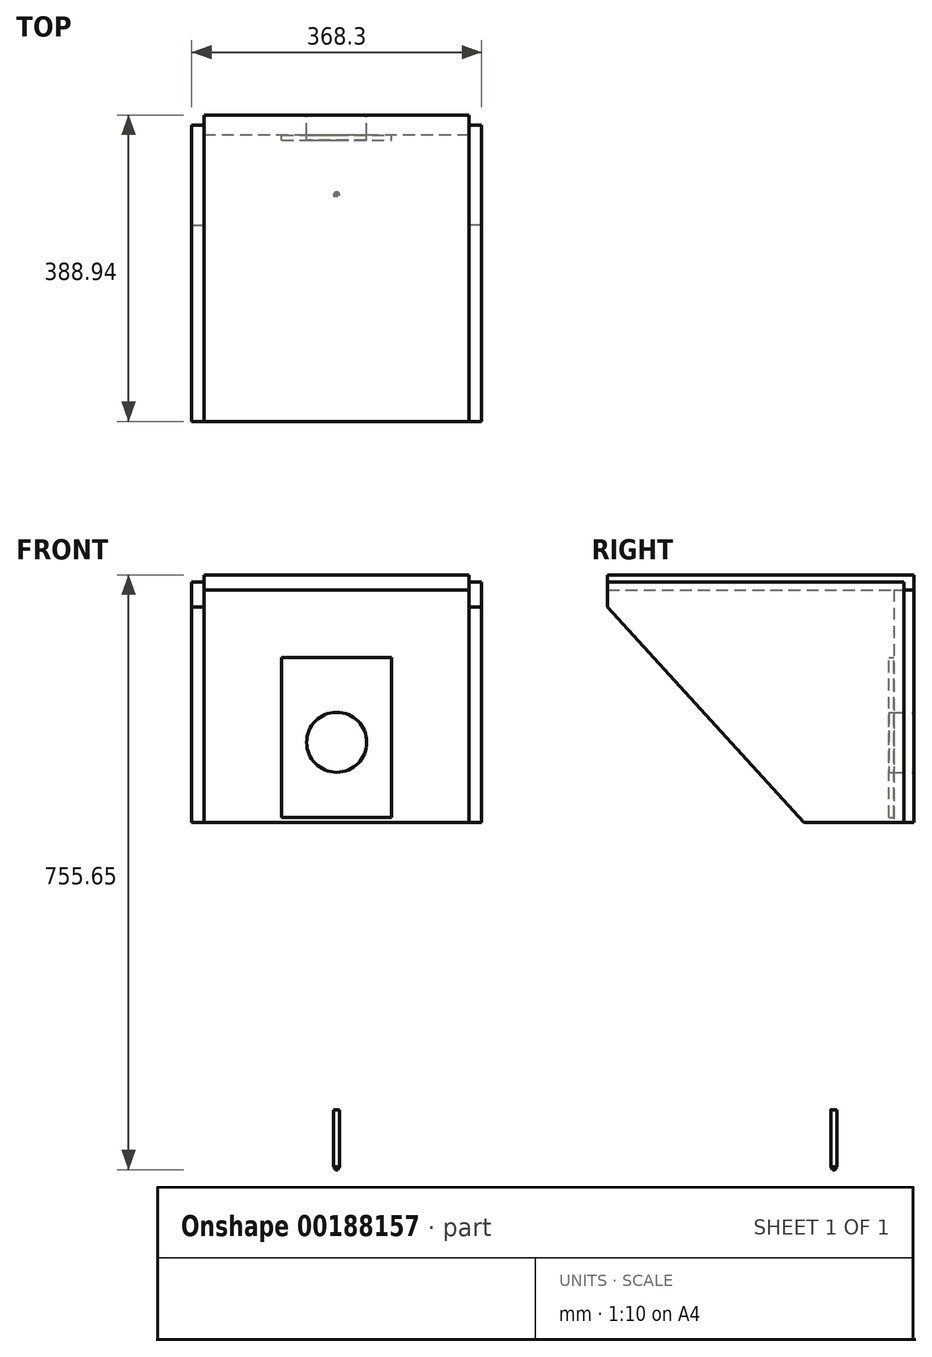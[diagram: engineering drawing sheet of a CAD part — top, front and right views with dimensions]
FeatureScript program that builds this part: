
annotation { "Feature Type Name" : "Feature", "Feature Type Description" : "" }
export const myFeature = defineFeature(function(context is Context, id is Id, definition is map)
    precondition{}
    {
        {
            var Q0;
            Q0=qCreatedBy(makeId("Top.planeOp"),FACE);
            var sketch = newSketch(context, id + "F0", { "sketchPlane" : qUnion([Q0])});
            skLineSegment(sketch, "E0.bottom", {"start": v(168.28, -194.47) * mm, "end": v(-168.28, -194.47) * mm});
            skLineSegment(sketch, "E0.top", {"start": v(168.28, 194.47) * mm, "end": v(-168.28, 194.47) * mm});
            skLineSegment(sketch, "E0.left", {"start": v(168.28, -194.47) * mm, "end": v(168.28, 194.47) * mm});
            skLineSegment(sketch, "E0.right", {"start": v(-168.28, -194.47) * mm, "end": v(-168.27, 194.47) * mm});
            skPoint(sketch, "E0.middle", {"position": v(0, 0) * mm});
            skSolve(sketch);
        }
        {
            var Q0;
            Q0=makeQuery(id+"F0.imprint","IMPRINT",FACE,{"disambiguationData":[TD([[makeQuery(id+"F0.imprint","IMPRINT",EDGE,{"derivedFrom":sQuery(id+"F0.wireOp",EDGE,"E0.bottom")}),-1.0]])]});
            extrude(context, id + "F1", {"entities" : qUnion([Q0]), "depth" : 19.05 * mm});
        }
        {
            var Q0;
            Q0=makeQuery(id+"F1.opExtrude","SWEPT_FACE",FACE,{"disambiguationData":[OSD([sQuery(id+"F0.wireOp",EDGE,"E0.top")])]});
            var sketch = newSketch(context, id + "F2", { "sketchPlane" : qUnion([Q0])});
            skLineSegment(sketch, "E1", {"start": v(-168.28, 0) * mm, "end": v(168.27, 0) * mm});
            skLineSegment(sketch, "E2", {"start": v(168.27, 0) * mm, "end": v(168.27, -295.28) * mm});
            skLineSegment(sketch, "E3", {"start": v(168.27, -295.28) * mm, "end": v(-168.28, -295.28) * mm});
            skLineSegment(sketch, "E4", {"start": v(-168.28, -295.27) * mm, "end": v(-168.28, 0) * mm});
            skCircle(sketch, "E5", {"center": v(0, -193.67) * mm, "radius": 38.1 * mm});
            skSolve(sketch);
        }
        {
            var Q0;
            Q0=makeQuery(id+"F2.imprint","IMPRINT",FACE,{"disambiguationData":[TD([[makeQuery(id+"F2.imprint","IMPRINT",EDGE,{"derivedFrom":sQuery(id+"F2.wireOp",EDGE,"E1")}),-1.0]])]});
            extrude(context, id + "F3", {"entities" : qUnion([Q0]), "oppositeDirection" : true, "depth" : 25.4 * mm});
        }
        {
            var Q0;
            Q0=makeQuery(id+"F1.opExtrude","SWEPT_FACE",FACE,{"disambiguationData":[OSD([sQuery(id+"F0.wireOp",EDGE,"E0.left")])]});
            var sketch = newSketch(context, id + "F4", { "sketchPlane" : qUnion([Q0])});
            skLineSegment(sketch, "E6", {"start": v(-194.47, 10.14) * mm, "end": v(-194.47, -21.61) * mm});
            skLineSegment(sketch, "E7", {"start": v(181.77, -295.27) * mm, "end": v(54.77, -295.27) * mm});
            skLineSegment(sketch, "E8", {"start": v(-194.47, -21.61) * mm, "end": v(54.77, -295.28) * mm});
            skLineSegment(sketch, "E9", {"start": v(-194.47, 10.14) * mm, "end": v(181.77, 10.14) * mm});
            skLineSegment(sketch, "E10", {"start": v(181.77, -295.27) * mm, "end": v(181.77, 10.14) * mm});
            skSolve(sketch);
        }
        {
            var Q0;
            Q0 = qSketchRegion(id + "F4", true);
            extrude(context, id + "F5", {"entities" : qUnion([Q0]), "depth" : 15.88 * mm});
        }
        {
            var Q0;
            Q0=makeQuery(id+"F5.opExtrude","SWEPT_BODY",BODY,{"disambiguationData":[OSD([sQuery(id+"F4.wireOp",EDGE,"E6"),sQuery(id+"F4.wireOp",EDGE,"E7"),sQuery(id+"F4.wireOp",EDGE,"E8"),sQuery(id+"F4.wireOp",EDGE,"E9"),sQuery(id+"F4.wireOp",EDGE,"E10")])]});
            var Q1;
            Q1=qCreatedBy(makeId("Right.planeOp"),FACE);
            mirror(context, id + "F6", {"entities" : qUnion([Q0]), "mirrorPlane" : qUnion([Q1])});
        }
        {
            var Q0;
            Q0=makeQuery(id+"F3.opExtrude","CAP_FACE",FACE,{"disambiguationData":[OSD([sQuery(id+"F2.wireOp",EDGE,"E1"),sQuery(id+"F2.wireOp",EDGE,"E2"),sQuery(id+"F2.wireOp",EDGE,"E3"),sQuery(id+"F2.wireOp",EDGE,"E4"),sQuery(id+"F2.wireOp",EDGE,"E5")])],"isStart":false});
            var sketch = newSketch(context, id + "F7", { "sketchPlane" : qUnion([Q0])});
            skLineSegment(sketch, "E11", {"start": v(-69.85, -288.93) * mm, "end": v(-69.85, -85.72) * mm});
            skLineSegment(sketch, "E12", {"start": v(-69.85, -288.93) * mm, "end": v(0, -288.93) * mm});
            skLineSegment(sketch, "E13", {"start": v(-69.85, -85.72) * mm, "end": v(0, -85.72) * mm});
            skLineSegment(sketch, "E14.MirrorCS", {"start": v(69.85, -288.93) * mm, "end": v(0, -288.93) * mm});
            skLineSegment(sketch, "E15.MirrorCS", {"start": v(69.85, -85.72) * mm, "end": v(0, -85.72) * mm});
            skLineSegment(sketch, "E16.MirrorCS", {"start": v(69.85, -288.93) * mm, "end": v(69.85, -85.72) * mm});
            skCircle(sketch, "E17", {"center": v(0, -193.67) * mm, "radius": 38.1 * mm});
            skSolve(sketch);
        }
        {
            var Q0;
            Q0 = qSketchRegion(id + "F7", true);
            extrude(context, id + "F8", {"entities" : qUnion([Q0]), "depth" : 6.35 * mm});
        }
        {
            var Q0;
            Q0=qCreatedBy(makeId("Right.planeOp"),FACE);
            var sketch = newSketch(context, id + "F9", { "sketchPlane" : qUnion([Q0])});
            skLineSegment(sketch, "E18", {"start": v(92.87, -660.4) * mm, "end": v(92.87, -736.6) * mm});
            skLineSegment(sketch, "E19", {"start": v(92.87, -736.6) * mm, "end": v(94.46, -736.6) * mm});
            skLineSegment(sketch, "E20", {"start": v(94.46, -736.6) * mm, "end": v(96.68, -732.75) * mm});
            skLineSegment(sketch, "E21", {"start": v(96.68, -732.75) * mm, "end": v(96.68, -660.4) * mm});
            skLineSegment(sketch, "E22", {"start": v(92.87, -660.4) * mm, "end": v(96.68, -660.4) * mm});
            skSolve(sketch);
        }
        {
            var Q0;
            Q0=makeQuery(id+"F9.imprint","IMPRINT",FACE,{"disambiguationData":[TD([[makeQuery(id+"F9.imprint","IMPRINT",EDGE,{"derivedFrom":sQuery(id+"F9.wireOp",EDGE,"E18")}),1.0]])]});
            var Q1;
            Q1=sQuery(id+"F9.wireOp",EDGE,"E18");
            revolve(context, id + "F10", {"entities" : qUnion([Q0]), "axis" : qUnion([Q1]), "revolveType" : RevolveType.FULL});
        }
    });
